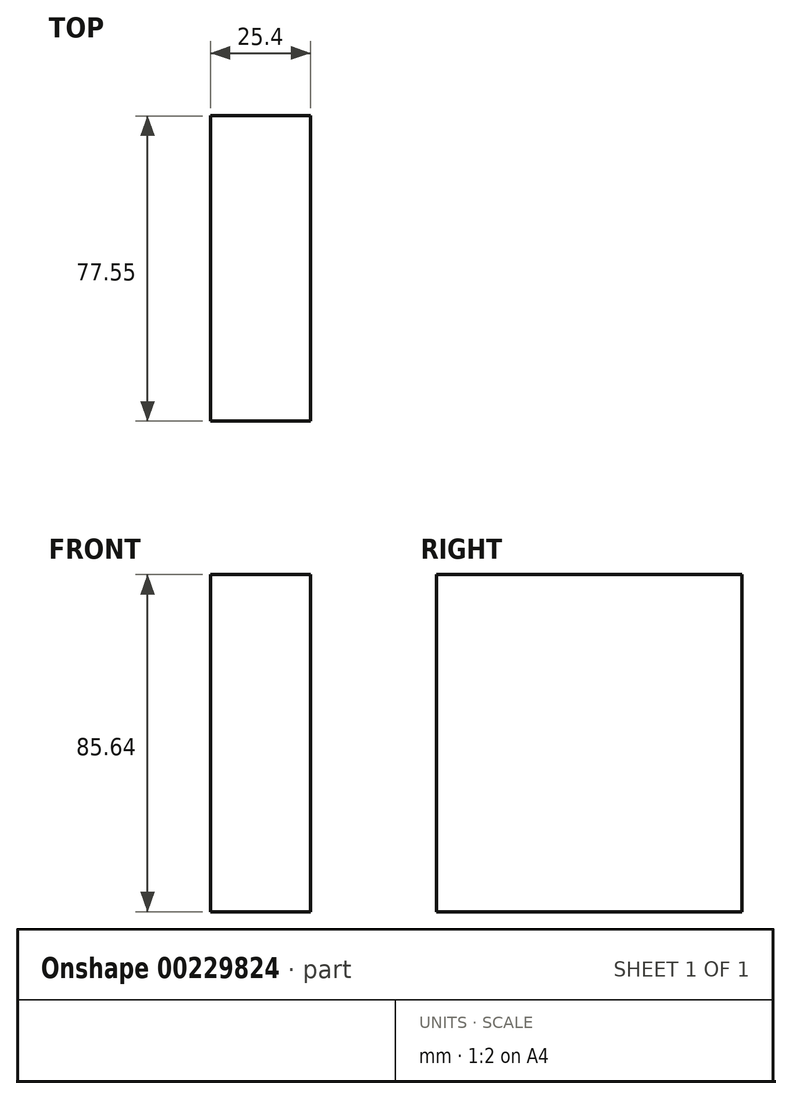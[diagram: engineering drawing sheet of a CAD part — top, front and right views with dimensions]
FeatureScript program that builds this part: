
annotation { "Feature Type Name" : "Feature", "Feature Type Description" : "" }
export const myFeature = defineFeature(function(context is Context, id is Id, definition is map)
    precondition{}
    {
        {
            var Q0;
            Q0=qCreatedBy(makeId("Right.planeOp"),FACE);
            var sketch = newSketch(context, id + "F0", { "sketchPlane" : qUnion([Q0])});
            skLineSegment(sketch, "E0.bottom", {"start": v(-45.3, 51.94) * mm, "end": v(32.25, 51.94) * mm});
            skLineSegment(sketch, "E0.top", {"start": v(-45.3, -33.7) * mm, "end": v(32.25, -33.7) * mm});
            skLineSegment(sketch, "E0.left", {"start": v(-45.3, 51.94) * mm, "end": v(-45.3, -33.7) * mm});
            skLineSegment(sketch, "E0.right", {"start": v(32.25, 51.94) * mm, "end": v(32.25, -33.7) * mm});
            skSolve(sketch);
        }
        {
            var Q0;
            Q0=makeQuery(id+"F0.imprint","IMPRINT",FACE,{"disambiguationData":[TD([[makeQuery(id+"F0.imprint","IMPRINT",EDGE,{"derivedFrom":sQuery(id+"F0.wireOp",EDGE,"E0.bottom")}),-1.0]])]});
            extrude(context, id + "F1", {"entities" : qUnion([Q0]), "oppositeDirection" : true, "depth" : 25.4 * mm});
        }
    });
